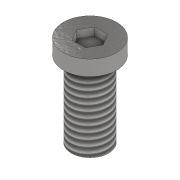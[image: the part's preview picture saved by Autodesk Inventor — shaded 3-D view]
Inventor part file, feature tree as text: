
AUTODESK INVENTOR PART (.ipt)
format: ipt  version: 2022 (Build 260153000, 153)  size: 124,416 bytes
history: native  units: mm
features: extrude x3, sketch x3, thread x1
ambient origin geometry x8: Origin, YZ Plane, XZ Plane, XY Plane, X Axis, Y Axis, Z Axis, Center Point
bodies: Solid1 (feature_tree)
feature tree (7):
  extrude  "Extrusion1"  Depth=10.0mm TaperAngle=0.0deg
  extrude  "Extrusion2"  Depth=2.0mm TaperAngle=0.0deg
  thread  "Thread1"  [1 undecoded]
  extrude  "Extrusion3"  Depth=1.0mm TaperAngle=0.0deg
  sketch  "Sketch1"  dims[d0=4.9mm d1=10.0mm d2=0.0mm]
  sketch  "Sketch2"  dims[d3=7.0mm d4=2.0mm d5=0.0mm d6=20.0mm d7=0.0mm]
  sketch  "Sketch3"  dims[d8=3.0mm d9=1.0mm d10=0.0mm]
note: 1 required parameter value undecoded (feature->parameter linkage not recoverable at this tier; creation-order binding heuristic only, values carry confidence <= 0.55)
